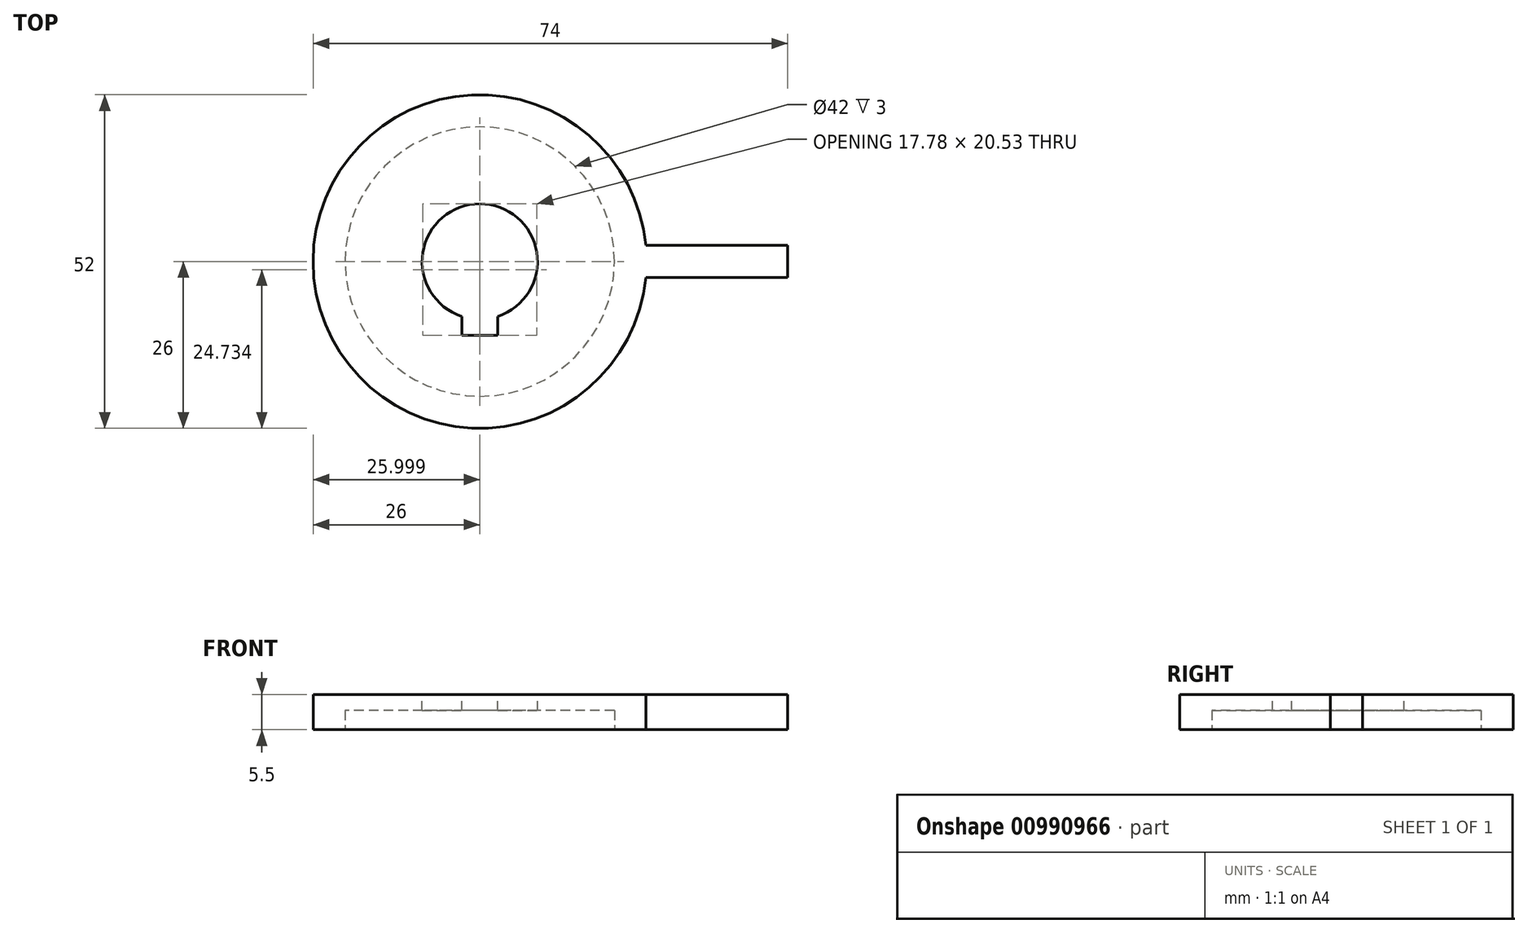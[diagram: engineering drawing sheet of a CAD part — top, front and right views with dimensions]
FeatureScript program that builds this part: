
annotation { "Feature Type Name" : "Feature", "Feature Type Description" : "" }
export const myFeature = defineFeature(function(context is Context, id is Id, definition is map)
    precondition{}
    {
        {
            var Q0;
            Q0=qCreatedBy(makeId("Top.planeOp"),FACE);
            var sketch = newSketch(context, id + "F0", { "sketchPlane" : qUnion([Q0])});
            skCircle(sketch, "E0", {"center": v(0, 0) * mm, "radius": 21 * mm});
            skCircle(sketch, "E1", {"center": v(0, 0) * mm, "radius": 26 * mm});
            skLineSegment(sketch, "E2", {"start": v(0, 0) * mm, "end": v(90.45, 0) * mm, "construction": true});
            skLineSegment(sketch, "E3", {"start": v(48, 0) * mm, "end": v(48, 2.5) * mm});
            skLineSegment(sketch, "E4", {"start": v(48, 2.5) * mm, "end": v(25.88, 2.5) * mm});
            skPoint(sketch, "E5", {"position": v(26, 0) * mm});
            skLineSegment(sketch, "E6.MirrorCS", {"start": v(48, -2.5) * mm, "end": v(25.88, -2.5) * mm});
            skLineSegment(sketch, "E7.MirrorCS", {"start": v(48, 0) * mm, "end": v(48, -2.5) * mm});
            skSolve(sketch);
        }
        {
            var Q0;
            Q0=makeQuery(id+"F0.imprint","IMPRINT",FACE,{"disambiguationData":[TD([[makeQuery(id+"F0.imprint","IMPRINT",EDGE,{"derivedFrom":sQuery(id+"F0.wireOp",EDGE,"E0")}),-1.0]])]});
            var Q1;
            Q1=makeQuery(id+"F0.imprint","IMPRINT",FACE,{"disambiguationData":[TD([[makeQuery(id+"F0.imprint","IMPRINT",EDGE,{"derivedFrom":sQuery(id+"F0.wireOp",EDGE,"E3")}),1.0]])]});
            var Q2;
            Q2=makeQuery(id+"F0.imprint","IMPRINT",FACE,{"disambiguationData":[TD([[makeQuery(id+"F0.imprint","IMPRINT",EDGE,{"derivedFrom":sQuery(id+"F0.wireOp",EDGE,"E0")}),1.0]])]});
            extrude(context, id + "F1", {"entities" : qUnion([Q0, Q1, Q2]), "depth" : 5.5 * mm, "offsetDistance" : 25 * mm});
        }
        {
            var Q0;
            Q0=makeQuery(id+"F0.imprint","IMPRINT",FACE,{"disambiguationData":[TD([[makeQuery(id+"F0.imprint","IMPRINT",EDGE,{"derivedFrom":sQuery(id+"F0.wireOp",EDGE,"E0")}),1.0]])]});
            extrude(context, id + "F2", {"entities" : qUnion([Q0]), "operationType" : NewBodyOperationType.REMOVE, "depth" : 3 * mm, "offsetDistance" : 25 * mm});
        }
        {
            var Q0;
            Q0=makeQuery(id+"F1.opExtrude","CAP_FACE",FACE,{"disambiguationData":[OSD([sQuery(id+"F0.wireOp",EDGE,"E1"),sQuery(id+"F0.wireOp",EDGE,"E3"),sQuery(id+"F0.wireOp",EDGE,"E4"),sQuery(id+"F0.wireOp",EDGE,"E6.MirrorCS"),sQuery(id+"F0.wireOp",EDGE,"E7.MirrorCS")])],"isStart":false});
            var sketch = newSketch(context, id + "F3", { "sketchPlane" : qUnion([Q0])});
            skCircle(sketch, "E8", {"center": v(0, 0) * mm, "radius": 9 * mm});
            skLineSegment(sketch, "E9", {"start": v(0, -11.53) * mm, "end": v(-2.8, -11.53) * mm});
            skLineSegment(sketch, "E10", {"start": v(-2.8, -11.53) * mm, "end": v(-2.8, -8.46) * mm});
            skLineSegment(sketch, "E11.MirrorCS", {"start": v(0, -11.53) * mm, "end": v(2.8, -11.53) * mm});
            skLineSegment(sketch, "E12.MirrorCS", {"start": v(2.8, -11.53) * mm, "end": v(2.8, -8.46) * mm});
            skPoint(sketch, "E13", {"position": v(0, -9.03) * mm});
            skSolve(sketch);
        }
        {
            var Q0;
            Q0=makeQuery(id+"F3.imprint","IMPRINT",FACE,{"disambiguationData":[TD([[makeQuery(id+"F3.imprint","IMPRINT",EDGE,{"derivedFrom":sQuery(id+"F3.wireOp",EDGE,"E8")}),1.0]])]});
            var Q1;
            {var subQ2=sQuery(id+"F3.wireOp",EDGE,"E9");Q1=makeQuery(id+"F3.imprint","IMPRINT",FACE,{"disambiguationData":[TD([[makeQuery(id+"F3.imprint","IMPRINT",EDGE,{"derivedFrom":subQ2}),-1.0]])]});}
            extrude(context, id + "F4", {"entities" : qUnion([Q0, Q1]), "operationType" : NewBodyOperationType.REMOVE, "endBound" : BoundingType.THROUGH_ALL, "oppositeDirection" : true, "depth" : 2 * mm, "offsetDistance" : 25 * mm});
        }
    });
